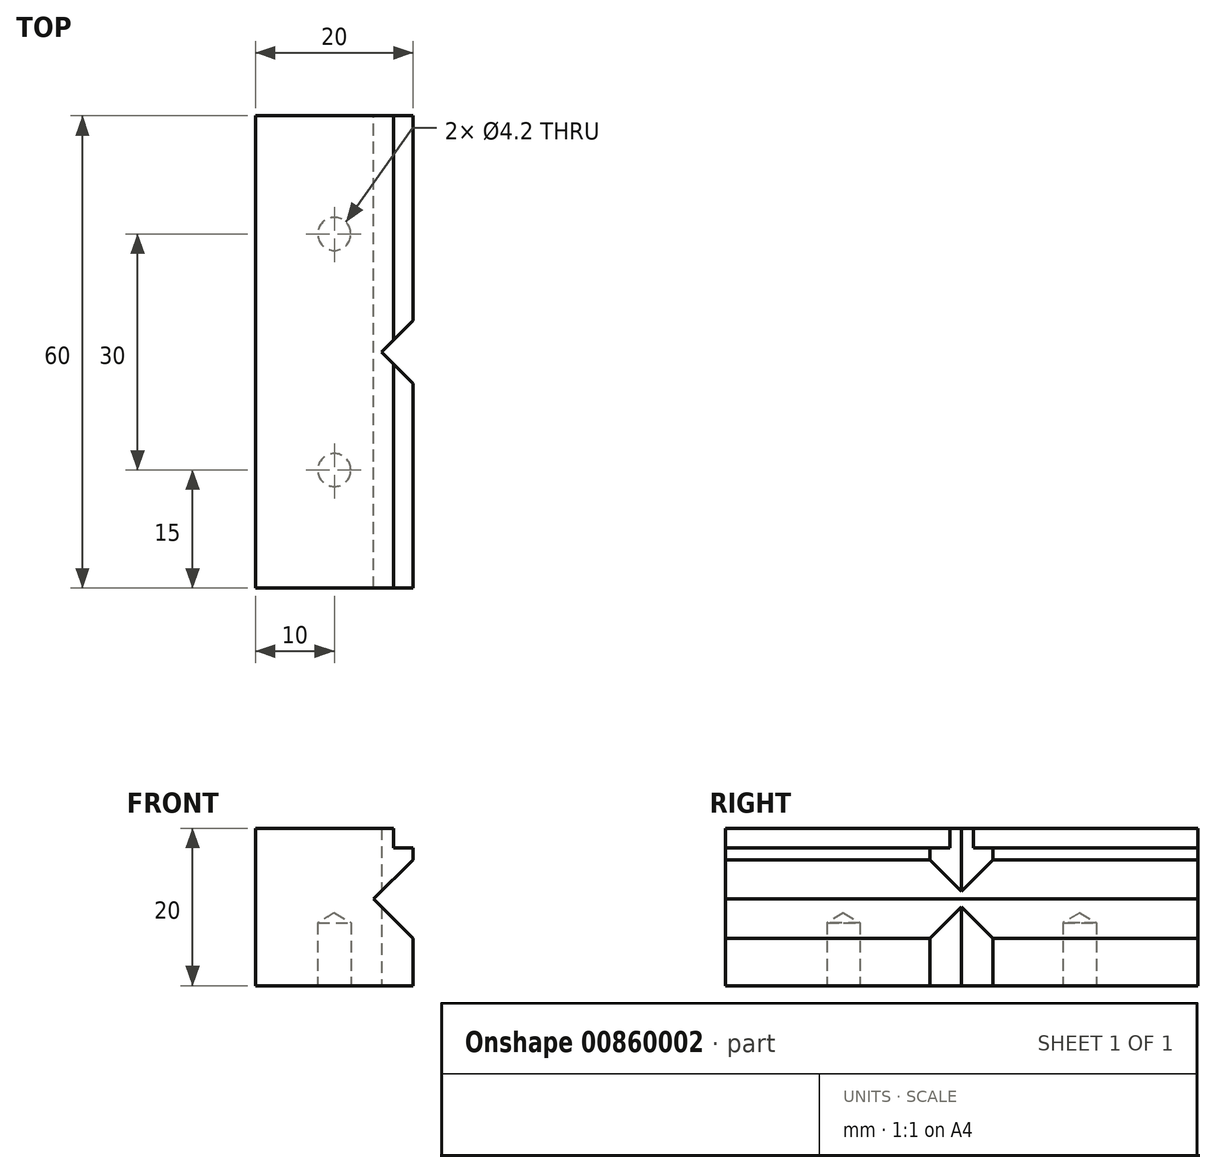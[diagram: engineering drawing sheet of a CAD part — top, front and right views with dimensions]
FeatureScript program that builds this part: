
annotation { "Feature Type Name" : "Feature", "Feature Type Description" : "" }
export const myFeature = defineFeature(function(context is Context, id is Id, definition is map)
    precondition{}
    {
        {
            var Q0;
            Q0=qCreatedBy(makeId("Front.planeOp"),FACE);
            var sketch = newSketch(context, id + "F0", { "sketchPlane" : qUnion([Q0])});
            skLineSegment(sketch, "E0.bottom", {"start": v(10, 0) * mm, "end": v(-10, 0) * mm});
            skLineSegment(sketch, "E0.top", {"start": v(7.5, 20) * mm, "end": v(-10, 20) * mm});
            skLineSegment(sketch, "E0.left", {"start": v(10, 0) * mm, "end": v(10, 6) * mm});
            skLineSegment(sketch, "E0.right", {"start": v(-10, 0) * mm, "end": v(-10, 20) * mm});
            skPoint(sketch, "E0.middle", {"position": v(0, 10) * mm});
            skLineSegment(sketch, "E1", {"start": v(7.5, 20) * mm, "end": v(7.5, 17.5) * mm});
            skLineSegment(sketch, "E2", {"start": v(7.5, 17.5) * mm, "end": v(10, 17.5) * mm});
            skLineSegment(sketch, "E3", {"start": v(10, 16) * mm, "end": v(5, 11) * mm});
            skLineSegment(sketch, "E4", {"start": v(5, 11) * mm, "end": v(10, 6) * mm});
            skLineSegment(sketch, "E5", {"start": v(5, 11) * mm, "end": v(10, 11) * mm, "construction": true});
            skPoint(sketch, "E6.orphan", {"position": v(10, 20) * mm});
            skLineSegment(sketch, "E7.trimOffspring", {"start": v(10, 16) * mm, "end": v(10, 17.5) * mm});
            skSolve(sketch);
        }
        {
            var Q0;
            Q0 = qSketchRegion(id + "F0", true);
            extrude(context, id + "F1", {"entities" : qUnion([Q0]), "depth" : 30 * mm, "offsetDistance" : 25 * mm});
        }
        {
            var Q0;
            Q0=makeQuery(id+"F1.opExtrude","SWEPT_FACE",FACE,{"disambiguationData":[OSD([sQuery(id+"F0.wireOp",EDGE,"E0.bottom")])]});
            var sketch = newSketch(context, id + "F2", { "sketchPlane" : qUnion([Q0])});
            skPoint(sketch, "E8", {"position": v(0, 15) * mm});
            skPoint(sketch, "E8.positionSnap0", {"position": v(-10, 15) * mm});
            skSolve(sketch);
        }
        {
            var Q0;
            Q0=sQuery(id+"F2.wireOp",VERTEX,"E8");
            var Q1;
            Q1=makeQuery(id+"F1.opExtrude","SWEPT_BODY",BODY,{"disambiguationData":[OSD([sQuery(id+"F0.wireOp",EDGE,"E0.bottom"),sQuery(id+"F0.wireOp",EDGE,"E0.top"),sQuery(id+"F0.wireOp",EDGE,"E0.left"),sQuery(id+"F0.wireOp",EDGE,"E0.right"),sQuery(id+"F0.wireOp",EDGE,"E1"),sQuery(id+"F0.wireOp",EDGE,"E2"),sQuery(id+"F0.wireOp",EDGE,"E3"),sQuery(id+"F0.wireOp",EDGE,"E4"),sQuery(id+"F0.wireOp",EDGE,"E7.trimOffspring")])]});
            hole(context, id + "F3", {"style" : HoleStyle.SIMPLE, "endStyle" : HoleEndStyle.BLIND, "standardTappedOrClearance" : lookupTablePath({ "standard" : "ISO", "engagement" : "75%", "pitch" : "0.8 mm", "size" : "M5", "type" : "Tapped" }), "standardBlindInLast" : lookupTablePath({ "standard" : "ISO", "engagement" : "75%", "pitch" : "0.8 mm", "size" : "M5", "type" : "Tapped" }), "holeDiameter" : 4.2 * mm, "majorDiameter" : 5 * mm, "showTappedDepth" : true, "holeDepth" : 8 * mm, "isTappedThrough" : true, "tappedDepth" : 6.4 * mm, "tapClearance" : 2, "startFromSketch" : true, "locations" : qUnion([Q0]), "scope" : qUnion([Q1])});
        }
        {
            var Q0;
            Q0=makeQuery(id+"F1.opExtrude","SWEPT_BODY",BODY,{"disambiguationData":[OSD([sQuery(id+"F0.wireOp",EDGE,"E0.bottom"),sQuery(id+"F0.wireOp",EDGE,"E0.top"),sQuery(id+"F0.wireOp",EDGE,"E0.left"),sQuery(id+"F0.wireOp",EDGE,"E0.right"),sQuery(id+"F0.wireOp",EDGE,"E1"),sQuery(id+"F0.wireOp",EDGE,"E2"),sQuery(id+"F0.wireOp",EDGE,"E3"),sQuery(id+"F0.wireOp",EDGE,"E4"),sQuery(id+"F0.wireOp",EDGE,"E7.trimOffspring")])]});
            var Q1;
            Q1=qCreatedBy(makeId("Front.planeOp"),FACE);
            mirror(context, id + "F4", {"operationType" : NewBodyOperationType.ADD, "entities" : qUnion([Q0]), "mirrorPlane" : qUnion([Q1])});
        }
        {
            var Q0;
            Q0=qCreatedBy(makeId("Top.planeOp"),FACE);
            var sketch = newSketch(context, id + "F5", { "sketchPlane" : qUnion([Q0])});
            skLineSegment(sketch, "E9", {"start": v(6, 0) * mm, "end": v(10, 4) * mm});
            skLineSegment(sketch, "E10", {"start": v(10, 4) * mm, "end": v(10, -4) * mm});
            skLineSegment(sketch, "E11", {"start": v(10, -4) * mm, "end": v(6, 0) * mm});
            skSolve(sketch);
        }
        {
            var Q0;
            Q0 = qSketchRegion(id + "F5", true);
            var Q1;
            {var subQ0=makeQuery(id+"F1.opExtrude","SWEPT_FACE",FACE,{"disambiguationData":[OSD([sQuery(id+"F0.wireOp",EDGE,"E0.top")])]});Q1=makeQuery(id+"F4.boolean.opBoolean","MERGE",FACE,{"derivedFrom":[subQ0,makeQuery(id+"F4.opPattern","COPY",FACE,{"derivedFrom":subQ0,"instanceName":"1"})]});}
            extrude(context, id + "F6", {"entities" : qUnion([Q0]), "operationType" : NewBodyOperationType.REMOVE, "endBound" : BoundingType.UP_TO_SURFACE, "depth" : 25 * mm, "endBoundEntityFace" : qUnion([Q1]), "offsetDistance" : 25 * mm});
        }
    });
